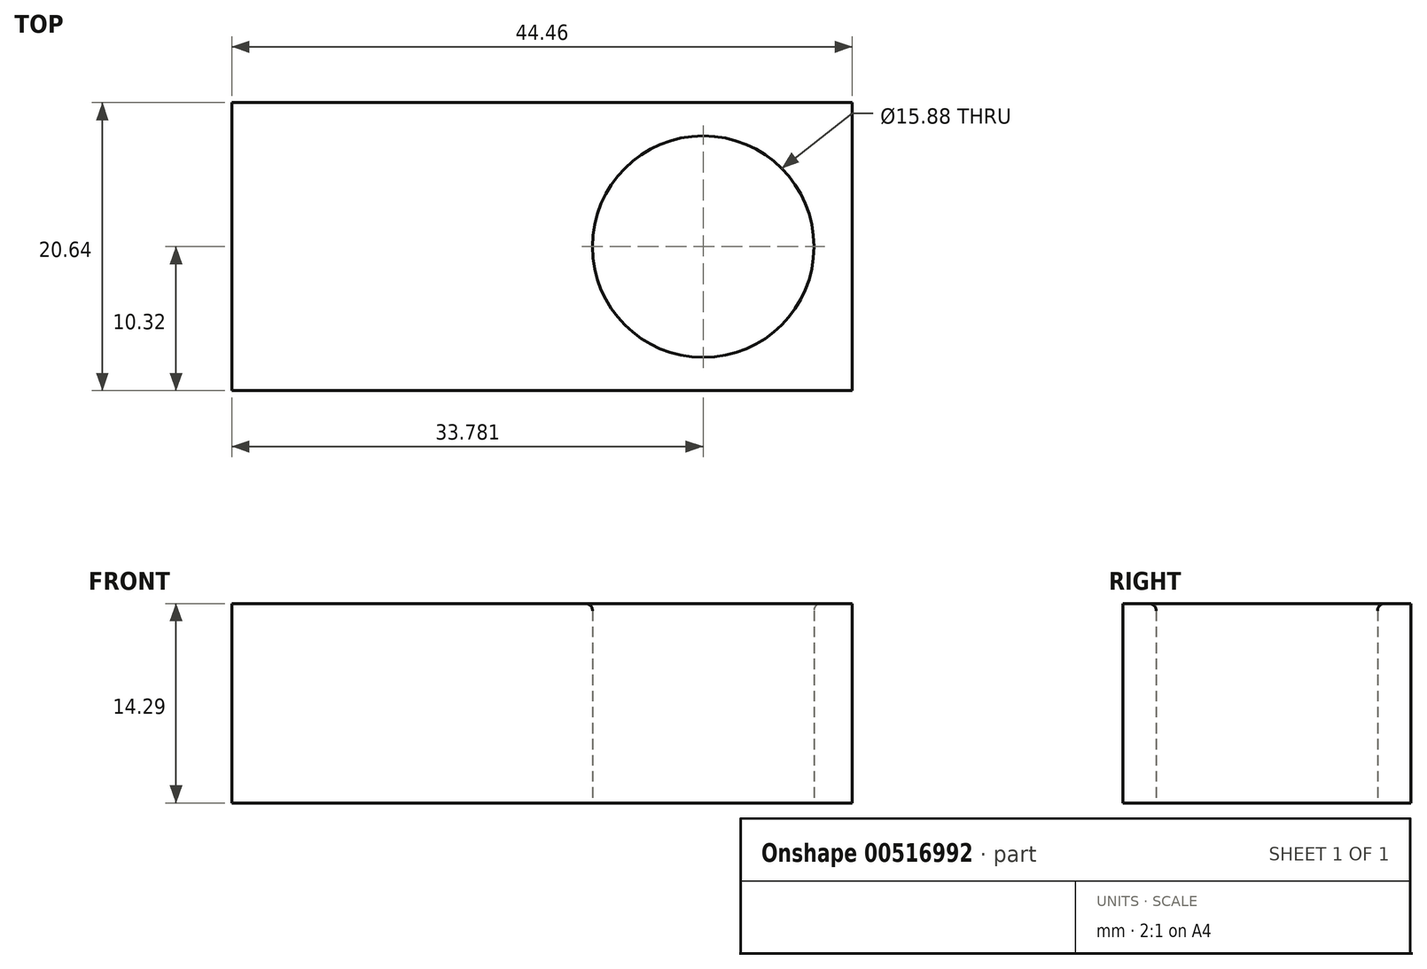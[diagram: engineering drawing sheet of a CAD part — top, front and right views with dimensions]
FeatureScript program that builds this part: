
annotation { "Feature Type Name" : "Feature", "Feature Type Description" : "" }
export const myFeature = defineFeature(function(context is Context, id is Id, definition is map)
    precondition{}
    {
        {
            var Q0;
            Q0=qCreatedBy(makeId("Top.planeOp"),FACE);
            var sketch = newSketch(context, id + "F0", { "sketchPlane" : qUnion([Q0])});
            skLineSegment(sketch, "E0.bottom", {"start": v(-22.23, 10.32) * mm, "end": v(22.23, 10.32) * mm});
            skLineSegment(sketch, "E0.top", {"start": v(-22.23, -10.32) * mm, "end": v(22.23, -10.32) * mm});
            skLineSegment(sketch, "E0.left", {"start": v(-22.22, 10.32) * mm, "end": v(-22.23, -10.32) * mm});
            skLineSegment(sketch, "E0.right", {"start": v(22.23, 10.32) * mm, "end": v(22.23, -10.32) * mm});
            skPoint(sketch, "E0.middle", {"position": v(0, 0) * mm});
            skCircle(sketch, "E1", {"center": v(-11.55, 0) * mm, "radius": 7.94 * mm});
            skCircle(sketch, "E2.MirrorC", {"center": v(11.55, 0) * mm, "radius": 7.94 * mm});
            skSolve(sketch);
        }
        {
            var Q0;
            Q0=makeQuery(id+"F0.imprint","IMPRINT",FACE,{"disambiguationData":[TD([[makeQuery(id+"F0.imprint","IMPRINT",EDGE,{"derivedFrom":sQuery(id+"F0.wireOp",EDGE,"E0.bottom")}),-1.0]])]});
            var Q1;
            Q1=makeQuery(id+"F0.imprint","IMPRINT",FACE,{"disambiguationData":[TD([[makeQuery(id+"F0.imprint","IMPRINT",EDGE,{"derivedFrom":sQuery(id+"F0.wireOp",EDGE,"E1")}),1.0]])]});
            var Q2;
            Q2=makeQuery(id+"F0.imprint","IMPRINT",FACE,{"disambiguationData":[TD([[makeQuery(id+"F0.imprint","IMPRINT",EDGE,{"derivedFrom":sQuery(id+"F0.wireOp",EDGE,"E2.MirrorC")}),-1.0]])]});
            extrude(context, id + "F1", {"entities" : qUnion([Q0, Q1, Q2]), "depth" : 1.59 * mm, "offsetDistance" : 25.4 * mm});
        }
        {
            var Q0;
            Q0=makeQuery(id+"F0.imprint","IMPRINT",FACE,{"disambiguationData":[TD([[makeQuery(id+"F0.imprint","IMPRINT",EDGE,{"derivedFrom":sQuery(id+"F0.wireOp",EDGE,"E1")}),1.0]])]});
            var Q1;
            Q1=makeQuery(id+"F0.imprint","IMPRINT",FACE,{"disambiguationData":[TD([[makeQuery(id+"F0.imprint","IMPRINT",EDGE,{"derivedFrom":sQuery(id+"F0.wireOp",EDGE,"E2.MirrorC")}),-1.0]])]});
            extrude(context, id + "F2", {"entities" : qUnion([Q0, Q1]), "operationType" : NewBodyOperationType.ADD, "depth" : 14.29 * mm, "offsetDistance" : 25.4 * mm});
        }
        {
            var Q0;
            Q0=makeQuery(id+"F2.opExtrude","CAP_EDGE",EDGE,{"disambiguationData":[OSD([sQuery(id+"F0.wireOp",EDGE,"E1")])],"isStart":false});
            var Q1;
            Q1=makeQuery(id+"F2.opExtrude","CAP_EDGE",EDGE,{"disambiguationData":[OSD([sQuery(id+"F0.wireOp",EDGE,"E2.MirrorC")])],"isStart":false});
            fillet(context, id + "F3", {"entities" : qUnion([Q0, Q1]), "radius" : .5 * mm, "tangentPropagation" : true, "allowEdgeOverflow" : false});
        }
    });
